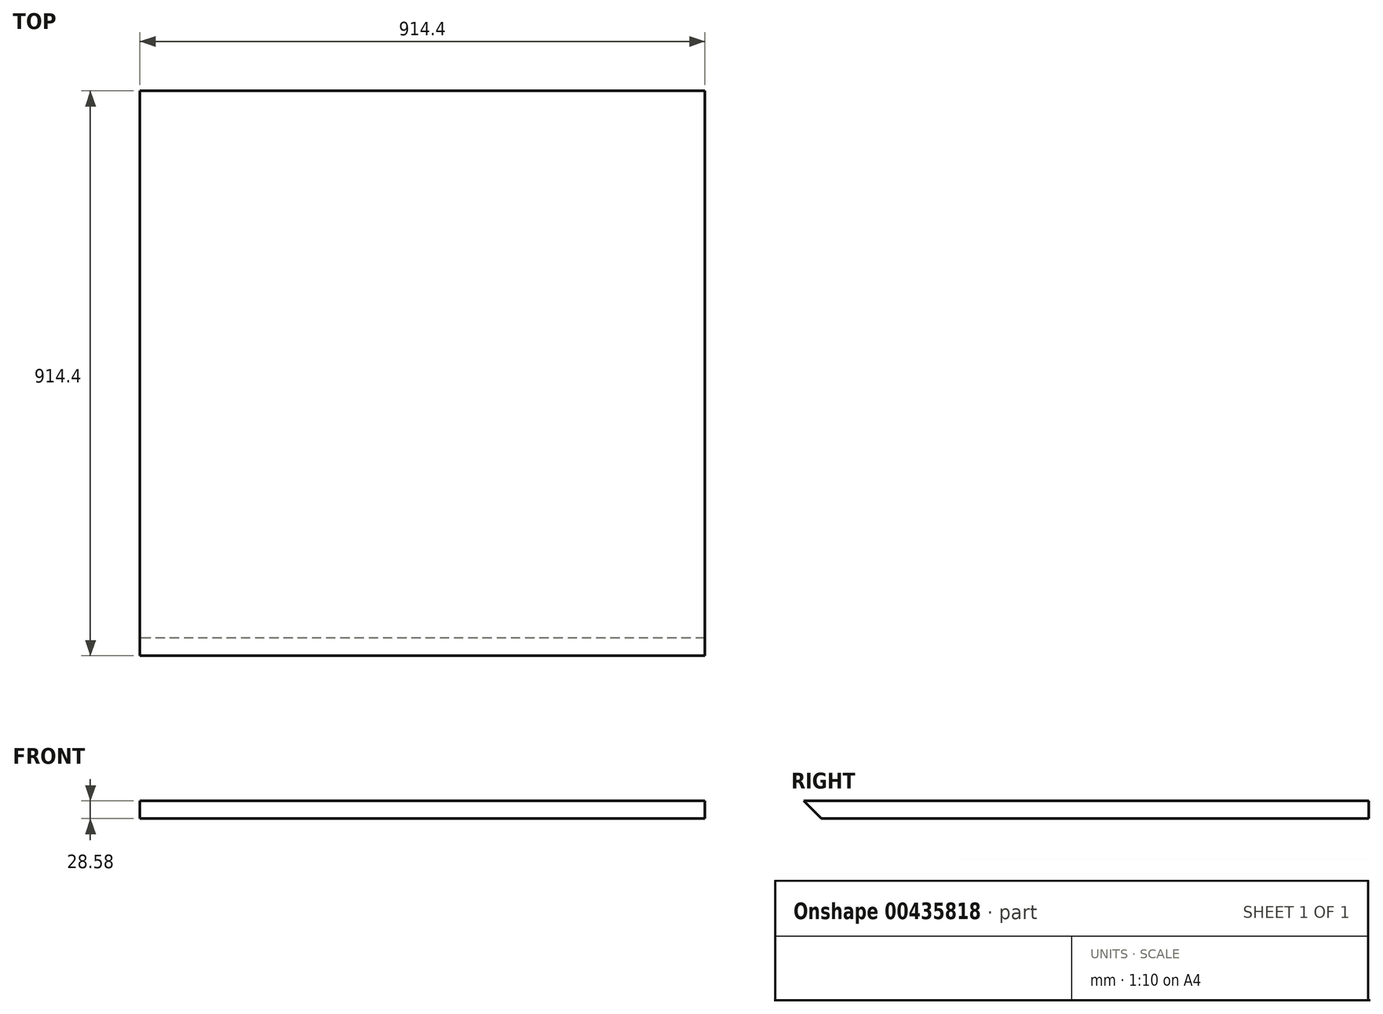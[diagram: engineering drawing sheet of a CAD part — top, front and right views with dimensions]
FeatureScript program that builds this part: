
annotation { "Feature Type Name" : "Feature", "Feature Type Description" : "" }
export const myFeature = defineFeature(function(context is Context, id is Id, definition is map)
    precondition{}
    {
        {
            var Q0;
            Q0=qCreatedBy(makeId("Right.planeOp"),FACE);
            var sketch = newSketch(context, id + "F0", { "sketchPlane" : qUnion([Q0])});
            skLineSegment(sketch, "E0.bottom", {"start": v(-428.63, -14.29) * mm, "end": v(457.2, -14.29) * mm});
            skLineSegment(sketch, "E0.top", {"start": v(-457.2, 14.29) * mm, "end": v(457.2, 14.29) * mm});
            skLineSegment(sketch, "E0.right", {"start": v(457.2, -14.29) * mm, "end": v(457.2, 14.29) * mm});
            skPoint(sketch, "E0.middle", {"position": v(0, 0) * mm});
            skLineSegment(sketch, "E1", {"start": v(-457.2, 14.29) * mm, "end": v(-428.63, -14.29) * mm});
            skSolve(sketch);
        }
        {
            var Q0;
            Q0=makeQuery(id+"F0.imprint","IMPRINT",FACE,{"disambiguationData":[TD([[makeQuery(id+"F0.imprint","IMPRINT",EDGE,{"derivedFrom":sQuery(id+"F0.wireOp",EDGE,"E0.bottom")}),1.0]])]});
            extrude(context, id + "F1", {"entities" : qUnion([Q0]), "endBound" : BoundingType.SYMMETRIC, "depth" : 914.4 * mm});
        }
    });
